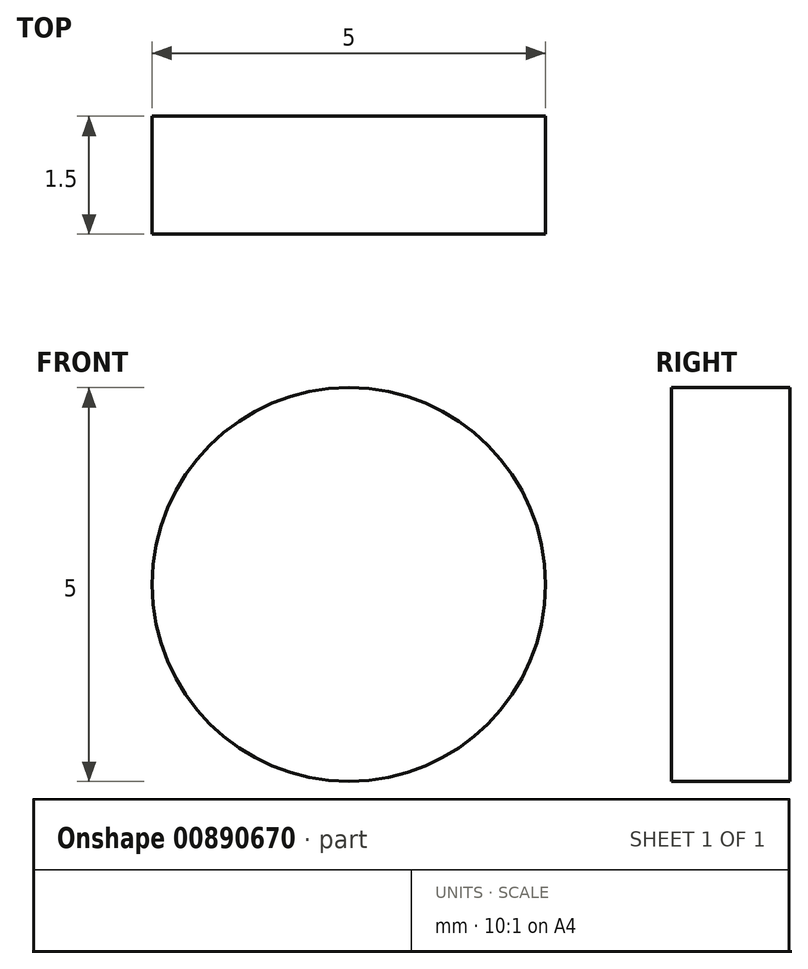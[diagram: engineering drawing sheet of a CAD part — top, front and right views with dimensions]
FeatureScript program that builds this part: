
annotation { "Feature Type Name" : "Feature", "Feature Type Description" : "" }
export const myFeature = defineFeature(function(context is Context, id is Id, definition is map)
    precondition{}
    {
        {
            var Q0;
            Q0=qCreatedBy(makeId("Front.planeOp"),FACE);
            var sketch = newSketch(context, id + "F0", { "sketchPlane" : qUnion([Q0])});
            skLineSegment(sketch, "E0.bottom", {"start": v(11, 30) * mm, "end": v(-11, 30) * mm, "construction": true});
            skLineSegment(sketch, "E0.top", {"start": v(11, -30) * mm, "end": v(-11, -30) * mm, "construction": true});
            skLineSegment(sketch, "E0.left", {"start": v(11, 30) * mm, "end": v(11, -30) * mm, "construction": true});
            skLineSegment(sketch, "E0.right", {"start": v(-11, 30) * mm, "end": v(-11, -30) * mm, "construction": true});
            skPoint(sketch, "E0.middle", {"position": v(0, 0) * mm});
            skCircle(sketch, "E1", {"center": v(-11, 30) * mm, "radius": 2.5 * mm});
            skCircle(sketch, "E2.MirrorC", {"center": v(11, 30) * mm, "radius": 2.5 * mm});
            skCircle(sketch, "E3.MirrorC", {"center": v(-11, -30) * mm, "radius": 2.5 * mm});
            skCircle(sketch, "E4.MirrorC", {"center": v(11, -30) * mm, "radius": 2.5 * mm});
            skLineSegment(sketch, "E5.0", {"start": v(19, 38) * mm, "end": v(19, 20) * mm});
            skLineSegment(sketch, "E5.1", {"start": v(19, 38) * mm, "end": v(-19, 38) * mm});
            skLineSegment(sketch, "E5.2", {"start": v(-19, 38) * mm, "end": v(-19, -38) * mm});
            skLineSegment(sketch, "E5.3", {"start": v(19, -38) * mm, "end": v(-19, -38) * mm});
            skLineSegment(sketch, "E6.bottom", {"start": v(1.75, -20) * mm, "end": v(-1.75, -20) * mm});
            skLineSegment(sketch, "E6.top", {"start": v(1.75, 20) * mm, "end": v(-1.75, 20) * mm});
            skLineSegment(sketch, "E6.left", {"start": v(1.75, -20) * mm, "end": v(1.75, 20) * mm});
            skLineSegment(sketch, "E6.right", {"start": v(-1.75, -20) * mm, "end": v(-1.75, 20) * mm});
            skLineSegment(sketch, "E7", {"start": v(1.75, 20) * mm, "end": v(19, 20) * mm});
            skLineSegment(sketch, "E8", {"start": v(1.75, -20) * mm, "end": v(19, -20) * mm});
            skLineSegment(sketch, "E9.trimOffspring", {"start": v(19, -20) * mm, "end": v(19, -38) * mm});
            skSolve(sketch);
        }
        {
            var Q0;
            Q0=makeQuery(id+"F0.imprint","IMPRINT",FACE,{"disambiguationData":[TD([[makeQuery(id+"F0.imprint","IMPRINT",EDGE,{"derivedFrom":sQuery(id+"F0.wireOp",EDGE,"E2.MirrorC")}),1.0]])]});
            extrude(context, id + "F1", {"entities" : qUnion([Q0]), "depth" : 1.5 * mm, "offsetDistance" : 25 * mm});
        }
    });
